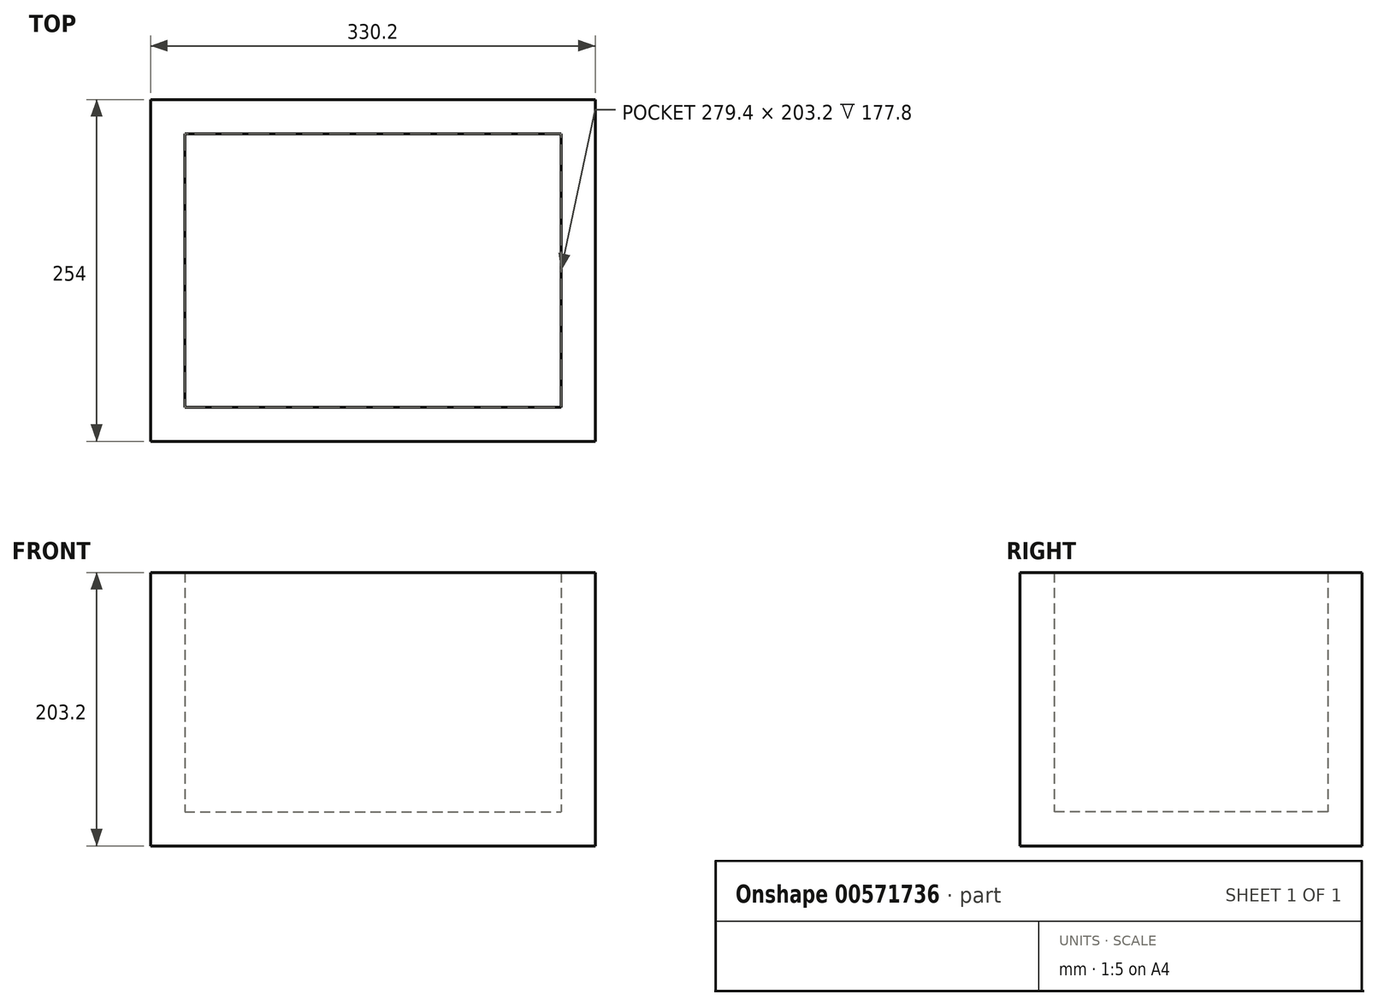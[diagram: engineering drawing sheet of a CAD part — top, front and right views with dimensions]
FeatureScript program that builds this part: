
annotation { "Feature Type Name" : "Feature", "Feature Type Description" : "" }
export const myFeature = defineFeature(function(context is Context, id is Id, definition is map)
    precondition{}
    {
        {
            var Q0;
            Q0=qCreatedBy(makeId("Top.planeOp"),FACE);
            var sketch = newSketch(context, id + "F0", { "sketchPlane" : qUnion([Q0])});
            skLineSegment(sketch, "E0.bottom", {"start": v(-165.1, 127) * mm, "end": v(165.1, 127) * mm});
            skLineSegment(sketch, "E0.top", {"start": v(-165.1, -127) * mm, "end": v(165.1, -127) * mm});
            skLineSegment(sketch, "E0.left", {"start": v(-165.1, 127) * mm, "end": v(-165.1, -127) * mm});
            skLineSegment(sketch, "E0.right", {"start": v(165.1, 127) * mm, "end": v(165.1, -127) * mm});
            skPoint(sketch, "E0.middle", {"position": v(0, 0) * mm});
            skSolve(sketch);
        }
        {
            var Q0;
            Q0=qSketchRegion(id+"F0",true);
            extrude(context, id + "F1", {"entities" : qUnion([Q0]), "depth" : 203.2 * mm, "offsetDistance" : 25.4 * mm});
        }
        {
            var Q0;
            Q0=makeQuery(id+"F1.opExtrude","CAP_FACE",FACE,{"disambiguationData":[OSD([sQuery(id+"F0.wireOp",EDGE,"E0.bottom"),sQuery(id+"F0.wireOp",EDGE,"E0.top"),sQuery(id+"F0.wireOp",EDGE,"E0.left"),sQuery(id+"F0.wireOp",EDGE,"E0.right")])],"isStart":false});
            shell(context, id + "F2", {"entities" : qUnion([Q0]), "thickness" : 25.4 * mm});
        }
    });
